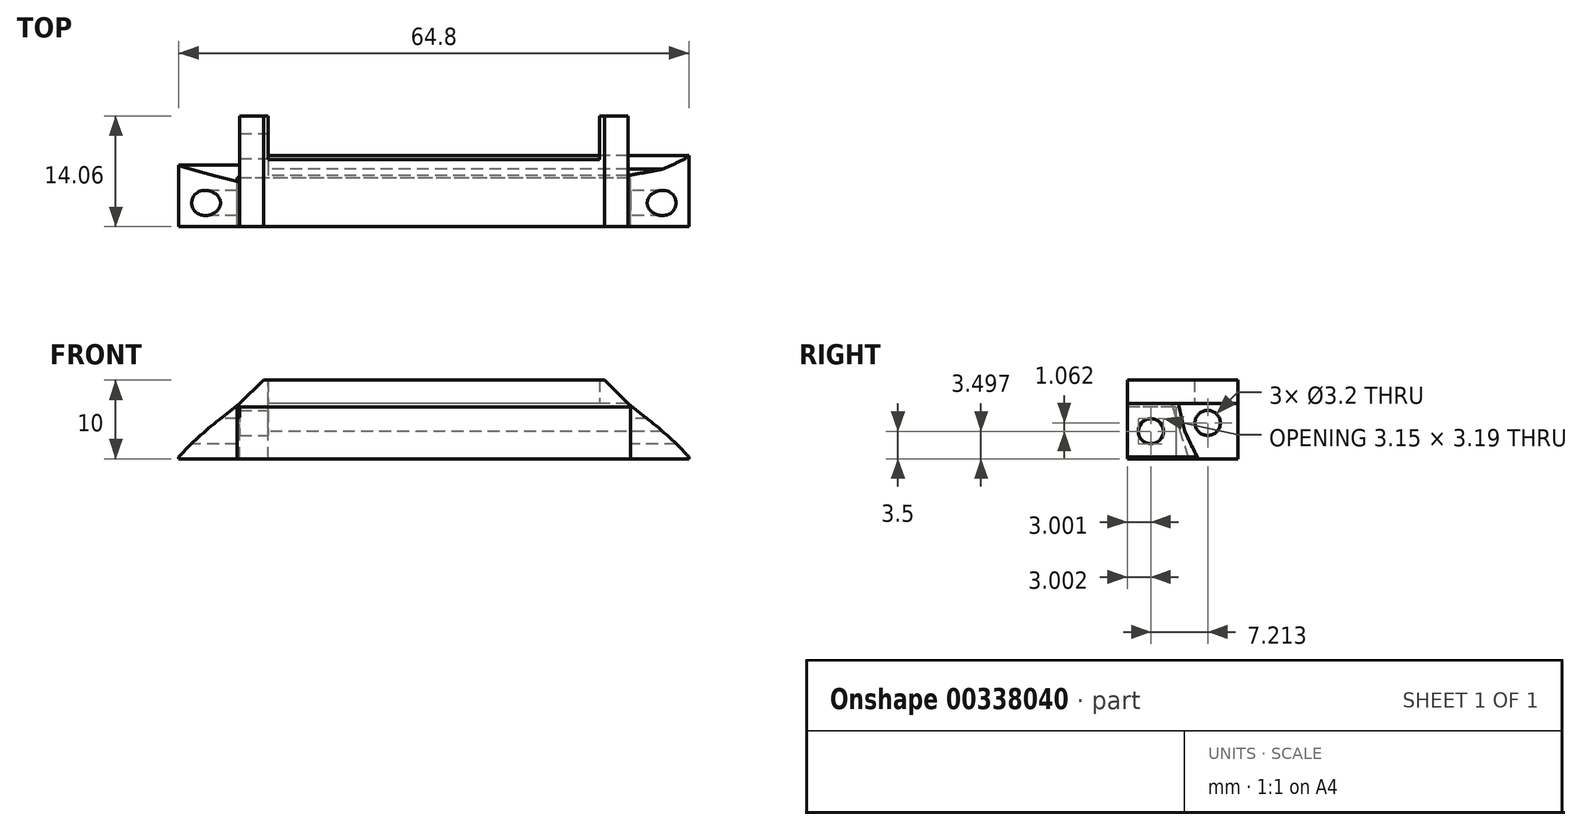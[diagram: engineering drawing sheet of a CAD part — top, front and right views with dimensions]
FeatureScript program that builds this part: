
annotation { "Feature Type Name" : "Feature", "Feature Type Description" : "" }
export const myFeature = defineFeature(function(context is Context, id is Id, definition is map)
    precondition{}
    {
        {
            var Q0;
            Q0=qCreatedBy(makeId("Right.planeOp"),FACE);
            cPlane(context, id + "F0", {"entities" : qUnion([Q0]), "cplaneType" : CPlaneType.OFFSET, "offset" : 40 * mm, "oppositeDirection" : true, "width" : 150 * mm, "height" : 150 * mm});
        }
        {
            var Q0;
            Q0=qCreatedBy(id+"F0.planeOp",FACE);
            var sketch = newSketch(context, id + "F1", { "sketchPlane" : qUnion([Q0])});
            skLineSegment(sketch, "E0.0", {"start": v(-62.06, 47) * mm, "end": v(-55.56, 47) * mm});
            skLineSegment(sketch, "E1.0", {"start": v(-62.06, 40) * mm, "end": v(-53.06, 40) * mm});
            skLineSegment(sketch, "E2", {"start": v(-62.06, 47) * mm, "end": v(-62.06, 40) * mm});
            skCircle(sketch, "E3", {"center": v(-59.06, 43.5) * mm, "radius": 1.6 * mm});
            skArc(sketch, "E4.0", {"start": v(-55.56, 47) * mm, "mid": v(-55.17, 45.25) * mm, "end": v(-54.76, 43.5) * mm});
            skArc(sketch, "E5.0", {"start": v(-53.06, 40) * mm, "mid": v(-53.92, 41.74) * mm, "end": v(-54.76, 43.5) * mm});
            skCircle(sketch, "E6", {"center": v(-59.06, 43.5) * mm, "radius": 3.25 * mm, "construction": true});
            skSolve(sketch);
        }
        {
            var Q0;
            Q0=qSketchRegion(id+"F1",true);
            extrude(context, id + "F2", {"entities" : qUnion([Q0]), "depth" : 33 * mm, "hasSecondDirection" : true, "secondDirectionOppositeDirection" : true, "secondDirectionDepth" : 33 * mm});
        }
        {
            var Q0;
            Q0=qCreatedBy(makeId("Front.planeOp"),FACE);
            var sketch = newSketch(context, id + "F3", { "sketchPlane" : qUnion([Q0])});
            skLineSegment(sketch, "E7", {"start": v(-40, 73.73) * mm, "end": v(-40, 20.27) * mm, "construction": true});
            skLineSegment(sketch, "E8.MirrorCS", {"start": v(-67.23, 45) * mm, "end": v(-64.65, 47) * mm});
            skArc(sketch, "E9.MirrorCS", {"start": v(-72.4, 40.2) * mm, "mid": v(-69.92, 42.72) * mm, "end": v(-67.23, 45) * mm});
            skLineSegment(sketch, "E10", {"start": v(-64.65, 47) * mm, "end": v(-77.52, 47) * mm});
            skLineSegment(sketch, "E11", {"start": v(-77.52, 47) * mm, "end": v(-77.52, 39.44) * mm});
            skLineSegment(sketch, "E12", {"start": v(-77.52, 39.44) * mm, "end": v(-72.4, 39.44) * mm});
            skLineSegment(sketch, "E13", {"start": v(-72.4, 39.44) * mm, "end": v(-72.4, 40.2) * mm});
            skLineSegment(sketch, "E14.MirrorCS", {"start": v(-7.6, 39.44) * mm, "end": v(-7.6, 40.2) * mm});
            skLineSegment(sketch, "E15.MirrorCS", {"start": v(-12.77, 45) * mm, "end": v(-15.35, 47) * mm});
            skLineSegment(sketch, "E16.MirrorCS", {"start": v(-2.48, 39.44) * mm, "end": v(-7.6, 39.44) * mm});
            skLineSegment(sketch, "E17.MirrorCS", {"start": v(-2.48, 47) * mm, "end": v(-2.48, 39.44) * mm});
            skArc(sketch, "E18.MirrorCS", {"start": v(-7.6, 40.2) * mm, "mid": v(-10.08, 42.72) * mm, "end": v(-12.77, 45) * mm});
            skLineSegment(sketch, "E19.MirrorCS", {"start": v(-15.35, 47) * mm, "end": v(-2.48, 47) * mm});
            skSolve(sketch);
        }
        {
            var Q0;
            Q0=qSketchRegion(id+"F3",true);
            extrude(context, id + "F4", {"entities" : qUnion([Q0]), "operationType" : NewBodyOperationType.REMOVE, "endBound" : BoundingType.THROUGH_ALL, "depth" : 25 * mm});
        }
        {
            var Q0;
            Q0=qCreatedBy(makeId("Front.planeOp"),FACE);
            cPlane(context, id + "F5", {"entities" : qUnion([Q0]), "cplaneType" : CPlaneType.OFFSET, "offset" : 48 * mm, "width" : 150 * mm, "height" : 150 * mm});
        }
        {
            var Q0;
            Q0=qCreatedBy(id+"F5.planeOp",FACE);
            var sketch = newSketch(context, id + "F6", { "sketchPlane" : qUnion([Q0])});
            skCircle(sketch, "E20", {"center": v(-62.85, 44.9) * mm, "radius": 1.8 * mm, "construction": true});
            skLineSegment(sketch, "E21", {"start": v(-64.65, 44.9) * mm, "end": v(-64.65, 47) * mm});
            skLineSegment(sketch, "E22", {"start": v(-64.65, 44.9) * mm, "end": v(-64.65, 40) * mm});
            skLineSegment(sketch, "E23", {"start": v(-62.85, 50.35) * mm, "end": v(-62.85, 37.67) * mm, "construction": true});
            skLineSegment(sketch, "E24.MirrorCS", {"start": v(-61.05, 44.9) * mm, "end": v(-61.05, 47) * mm});
            skLineSegment(sketch, "E25.MirrorCS", {"start": v(-61.05, 44.9) * mm, "end": v(-61.05, 40) * mm});
            skLineSegment(sketch, "E26", {"start": v(-61.05, 47) * mm, "end": v(-64.65, 47) * mm});
            skLineSegment(sketch, "E27", {"start": v(-64.65, 40) * mm, "end": v(-61.05, 40) * mm});
            skSolve(sketch);
        }
        {
            var Q0;
            Q0=qSketchRegion(id+"F6",true);
            extrude(context, id + "F7", {"entities" : qUnion([Q0]), "operationType" : NewBodyOperationType.ADD, "endBound" : BoundingType.UP_TO_NEXT, "depth" : 25 * mm});
        }
        {
            var Q0;
            Q0=qCreatedBy(id+"F0.planeOp",FACE);
            var sketch = newSketch(context, id + "F8", { "sketchPlane" : qUnion([Q0])});
            skLineSegment(sketch, "E28.bottom", {"start": v(-55.86, 46.6) * mm, "end": v(-62.16, 46.6) * mm});
            skLineSegment(sketch, "E28.top", {"start": v(-55.86, 39.6) * mm, "end": v(-62.16, 39.6) * mm});
            skLineSegment(sketch, "E28.left", {"start": v(-55.86, 46.6) * mm, "end": v(-55.86, 39.6) * mm});
            skLineSegment(sketch, "E28.right", {"start": v(-62.16, 46.6) * mm, "end": v(-62.16, 39.6) * mm});
            skSolve(sketch);
        }
        {
            var Q0;
            Q0=qSketchRegion(id+"F8",true);
            extrude(context, id + "F9", {"entities" : qUnion([Q0]), "operationType" : NewBodyOperationType.REMOVE, "oppositeDirection" : true, "depth" : 25 * mm, "hasSecondDirection" : true, "secondDirectionOppositeDirection" : false, "secondDirectionDepth" : 25 * mm});
        }
        {
            var Q0;
            Q0=qCreatedBy(id+"F0.planeOp",FACE);
            var sketch = newSketch(context, id + "F10", { "sketchPlane" : qUnion([Q0])});
            skCircle(sketch, "E29", {"center": v(-51.84, 44.56) * mm, "radius": 1.6 * mm});
            skSolve(sketch);
        }
        {
            var Q0;
            Q0=qSketchRegion(id+"F10",true);
            extrude(context, id + "F11", {"entities" : qUnion([Q0]), "operationType" : NewBodyOperationType.REMOVE, "endBound" : BoundingType.THROUGH_ALL, "oppositeDirection" : true, "depth" : 25 * mm, "hasSecondDirection" : true, "secondDirectionBound" : SecondDirectionBoundingType.THROUGH_ALL, "secondDirectionOppositeDirection" : false, "secondDirectionDepth" : 25 * mm});
        }
        {
            var Q0;
            {var subQ0=sQuery(id+"F6.wireOp",EDGE,"E26");Q0=makeQuery(id+"FYnT0MVXlafkFCY_3.1.F7.boolean.opBoolean","MERGE",FACE,{"derivedFrom":[makeQuery(id+"F7.boolean.opBoolean","MERGE",FACE,{"derivedFrom":[makeQuery(id+"F2.opExtrude","SWEPT_FACE",FACE,{"disambiguationData":[OSD([sQuery(id+"F1.wireOp",EDGE,"E0.0")])]}),makeQuery(id+"F7.opExtrude","SWEPT_FACE",FACE,{"disambiguationData":[OSD([subQ0])]})]}),makeQuery(id+"FYnT0MVXlafkFCY_3.1.F7.opExtrude","SWEPT_FACE",FACE,{"disambiguationData":[OSD([subQ0])]})]});}
            var sketch = newSketch(context, id + "F12", { "sketchPlane" : qUnion([Q0])});
            skLineSegment(sketch, "E30.0.0", {"start": v(-64.65, -55.56) * mm, "end": v(-64.65, -62.06) * mm});
            skLineSegment(sketch, "E30.0.1", {"start": v(-64.65, -62.06) * mm, "end": v(-15.35, -62.06) * mm});
            skLineSegment(sketch, "E30.0.2", {"start": v(-15.35, -62.06) * mm, "end": v(-15.35, -55.56) * mm});
            skLineSegment(sketch, "E30.0.3", {"start": v(-15.35, -55.56) * mm, "end": v(-15.35, -48) * mm});
            skLineSegment(sketch, "E30.0.4", {"start": v(-15.35, -48) * mm, "end": v(-18.95, -48) * mm});
            skLineSegment(sketch, "E30.0.5", {"start": v(-18.95, -48) * mm, "end": v(-18.95, -55.56) * mm});
            skLineSegment(sketch, "E30.0.6", {"start": v(-18.95, -55.56) * mm, "end": v(-61.05, -55.56) * mm});
            skLineSegment(sketch, "E30.0.7", {"start": v(-61.05, -55.56) * mm, "end": v(-61.05, -48) * mm});
            skLineSegment(sketch, "E30.0.8", {"start": v(-61.05, -48) * mm, "end": v(-64.65, -48) * mm});
            skLineSegment(sketch, "E30.0.9", {"start": v(-64.65, -48) * mm, "end": v(-64.65, -55.56) * mm});
            skSolve(sketch);
        }
        {
            var Q0;
            Q0 = qSketchRegion(id + "F12", true);
            extrude(context, id + "F13", {"entities" : qUnion([Q0]), "operationType" : NewBodyOperationType.ADD, "depth" : 3 * mm});
        }
        {
            var Q0;
            Q0=makeQuery(id+"F13.opExtrude","SWEPT_FACE",FACE,{"disambiguationData":[OSD([sQuery(id+"F12.wireOp",EDGE,"E30.0.6")])]});
            var sketch = newSketch(context, id + "F14", { "sketchPlane" : qUnion([Q0])});
            skLineSegment(sketch, "E31.0.0", {"start": v(18.95, 47) * mm, "end": v(61.05, 47) * mm});
            skLineSegment(sketch, "E31.0.1", {"start": v(61.05, 47) * mm, "end": v(61.05, 50) * mm});
            skLineSegment(sketch, "E31.0.2", {"start": v(61.05, 50) * mm, "end": v(18.95, 50) * mm});
            skLineSegment(sketch, "E31.0.3", {"start": v(18.95, 50) * mm, "end": v(18.95, 47) * mm});
            skSolve(sketch);
        }
        {
            var Q0;
            Q0 = qSketchRegion(id + "F14", true);
            extrude(context, id + "F15", {"entities" : qUnion([Q0]), "operationType" : NewBodyOperationType.ADD, "depth" : 2 * mm});
        }
        {
            var Q0;
            Q0=makeQuery(id+"F13.opExtrude","CAP_EDGE",EDGE,{"disambiguationData":[OSD([sQuery(id+"F12.wireOp",EDGE,"E30.0.0"),sQuery(id+"F12.wireOp",EDGE,"E30.0.9")])],"isStart":false});
            var Q1;
            Q1=makeQuery(id+"F13.opExtrude","CAP_EDGE",EDGE,{"disambiguationData":[OSD([sQuery(id+"F12.wireOp",EDGE,"E30.0.2"),sQuery(id+"F12.wireOp",EDGE,"E30.0.3")])],"isStart":false});
            chamfer(context, id + "F16", {"entities" : qUnion([Q0, Q1]), "width" : 3 * mm, "tangentPropagation" : true});
        }
        {
            var Q0;
            Q0=makeQuery(id+"F13.boolean.opBoolean","MERGE",FACE,{"derivedFrom":[makeQuery(id+"F7.opExtrude","SWEPT_FACE",FACE,{"disambiguationData":[OSD([sQuery(id+"F6.wireOp",EDGE,"E21"),sQuery(id+"F6.wireOp",EDGE,"E22")])]}),makeQuery(id+"F13.opExtrude","SWEPT_FACE",FACE,{"disambiguationData":[OSD([sQuery(id+"F12.wireOp",EDGE,"E30.0.0"),sQuery(id+"F12.wireOp",EDGE,"E30.0.9")])]})]});
            var sketch = newSketch(context, id + "F17", { "sketchPlane" : qUnion([Q0])});
            skLineSegment(sketch, "E32", {"start": v(55.56, 47) * mm, "end": v(53.06, 40) * mm});
            skLineSegment(sketch, "E33", {"start": v(53.06, 40) * mm, "end": v(54.22, 40) * mm});
            skLineSegment(sketch, "E34", {"start": v(54.22, 40) * mm, "end": v(56.4, 47) * mm});
            skLineSegment(sketch, "E35", {"start": v(56.4, 47) * mm, "end": v(55.56, 47) * mm});
            skSolve(sketch);
        }
        {
            var Q0;
            Q0 = qSketchRegion(id + "F17", true);
            extrude(context, id + "F18", {"entities" : qUnion([Q0]), "operationType" : NewBodyOperationType.REMOVE, "depth" : 25 * mm});
        }
    });
